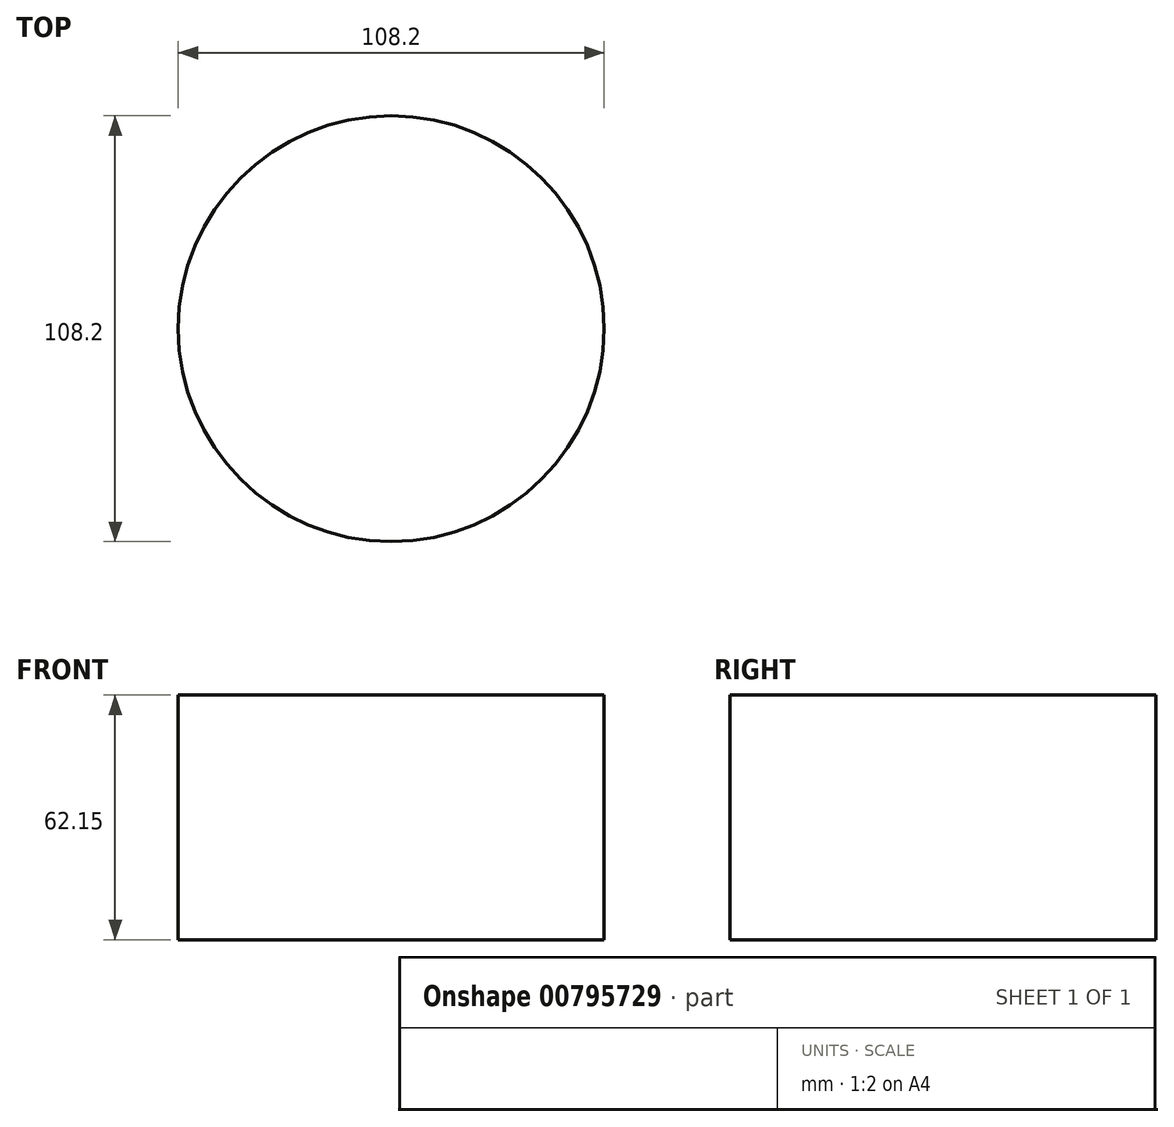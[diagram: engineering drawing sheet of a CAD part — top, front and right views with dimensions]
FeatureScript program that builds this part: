
annotation { "Feature Type Name" : "Feature", "Feature Type Description" : "" }
export const myFeature = defineFeature(function(context is Context, id is Id, definition is map)
    precondition{}
    {
        {
            var Q0;
            Q0=qCreatedBy(makeId("Front.planeOp"),FACE);
            var sketch = newSketch(context, id + "F0", { "sketchPlane" : qUnion([Q0])});
            skLineSegment(sketch, "E0.bottom", {"start": v(0, 0) * mm, "end": v(54.1, 0) * mm});
            skLineSegment(sketch, "E0.top", {"start": v(0, 62.15) * mm, "end": v(54.1, 62.15) * mm});
            skLineSegment(sketch, "E0.left", {"start": v(0, 0) * mm, "end": v(0, 62.15) * mm});
            skLineSegment(sketch, "E0.right", {"start": v(54.1, 0) * mm, "end": v(54.1, 62.15) * mm});
            skSolve(sketch);
        }
        {
            var Q0;
            Q0=makeQuery(id+"F0.imprint","IMPRINT",FACE,{"disambiguationData":[TD([[makeQuery(id+"F0.imprint","IMPRINT",EDGE,{"derivedFrom":sQuery(id+"F0.wireOp",EDGE,"E0.bottom")}),1.0]])]});
            var Q1;
            Q1=sQuery(id+"F0.wireOp",EDGE,"E0.left");
            revolve(context, id + "F1", {"surfaceOperationType" : NewSurfaceOperationType.NEW, "entities" : qUnion([Q0]), "axis" : qUnion([Q1]), "revolveType" : RevolveType.FULL});
        }
    });
